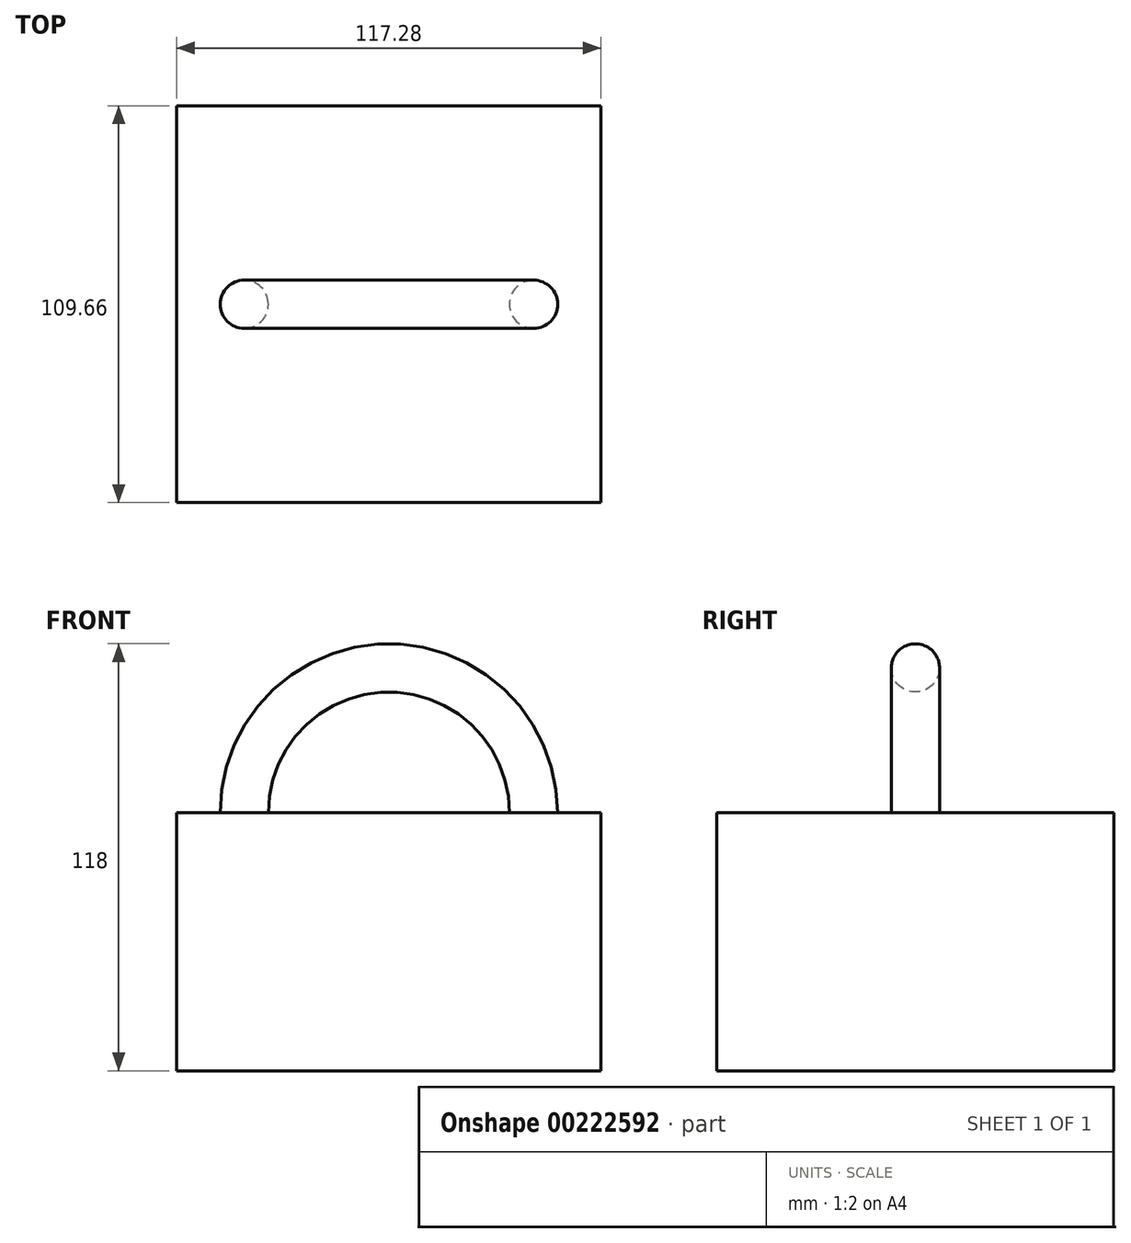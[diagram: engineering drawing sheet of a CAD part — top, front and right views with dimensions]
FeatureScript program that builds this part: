
annotation { "Feature Type Name" : "Feature", "Feature Type Description" : "" }
export const myFeature = defineFeature(function(context is Context, id is Id, definition is map)
    precondition{}
    {
        {
            var Q0;
            Q0=qCreatedBy(makeId("Top.planeOp"),FACE);
            var sketch = newSketch(context, id + "F0", { "sketchPlane" : qUnion([Q0])});
            skLineSegment(sketch, "E0.bottom", {"start": v(58.64, -54.83) * mm, "end": v(-58.64, -54.83) * mm});
            skLineSegment(sketch, "E0.top", {"start": v(58.64, 54.83) * mm, "end": v(-58.64, 54.83) * mm});
            skLineSegment(sketch, "E0.left", {"start": v(58.64, -54.83) * mm, "end": v(58.64, 54.83) * mm});
            skLineSegment(sketch, "E0.right", {"start": v(-58.64, -54.83) * mm, "end": v(-58.64, 54.83) * mm});
            skPoint(sketch, "E0.middle", {"position": v(0, 0) * mm});
            skSolve(sketch);
        }
        {
            var Q0;
            Q0=qCreatedBy(makeId("Top.planeOp"),FACE);
            var sketch = newSketch(context, id + "F1", { "sketchPlane" : qUnion([Q0])});
            skCircle(sketch, "E1", {"center": v(39.96, 0) * mm, "radius": 6.66 * mm});
            skSolve(sketch);
        }
        {
            var Q0;
            Q0 = qSketchRegion(id + "F0", true);
            extrude(context, id + "F2", {"entities" : qUnion([Q0]), "oppositeDirection" : true, "depth" : 71.37 * mm});
        }
        {
            var Q0;
            Q0=qCreatedBy(makeId("Top.planeOp"),FACE);
            var sketch = newSketch(context, id + "F3", { "sketchPlane" : qUnion([Q0])});
            skLineSegment(sketch, "E2", {"start": v(0, 55.2) * mm, "end": v(0, -55.48) * mm});
            skSolve(sketch);
        }
        {
            var Q0;
            Q0=makeQuery(id+"F1.imprint","IMPRINT",FACE,{"disambiguationData":[TD([[makeQuery(id+"F1.imprint","IMPRINT",EDGE,{"derivedFrom":sQuery(id+"F1.wireOp",EDGE,"E1")}),1.0]])]});
            var Q1;
            Q1=sQuery(id+"F3.wireOp",EDGE,"E2");
            revolve(context, id + "F4", {"operationType" : NewBodyOperationType.ADD, "entities" : qUnion([Q0]), "axis" : qUnion([Q1]), "revolveType" : RevolveType.FULL});
        }
    });
